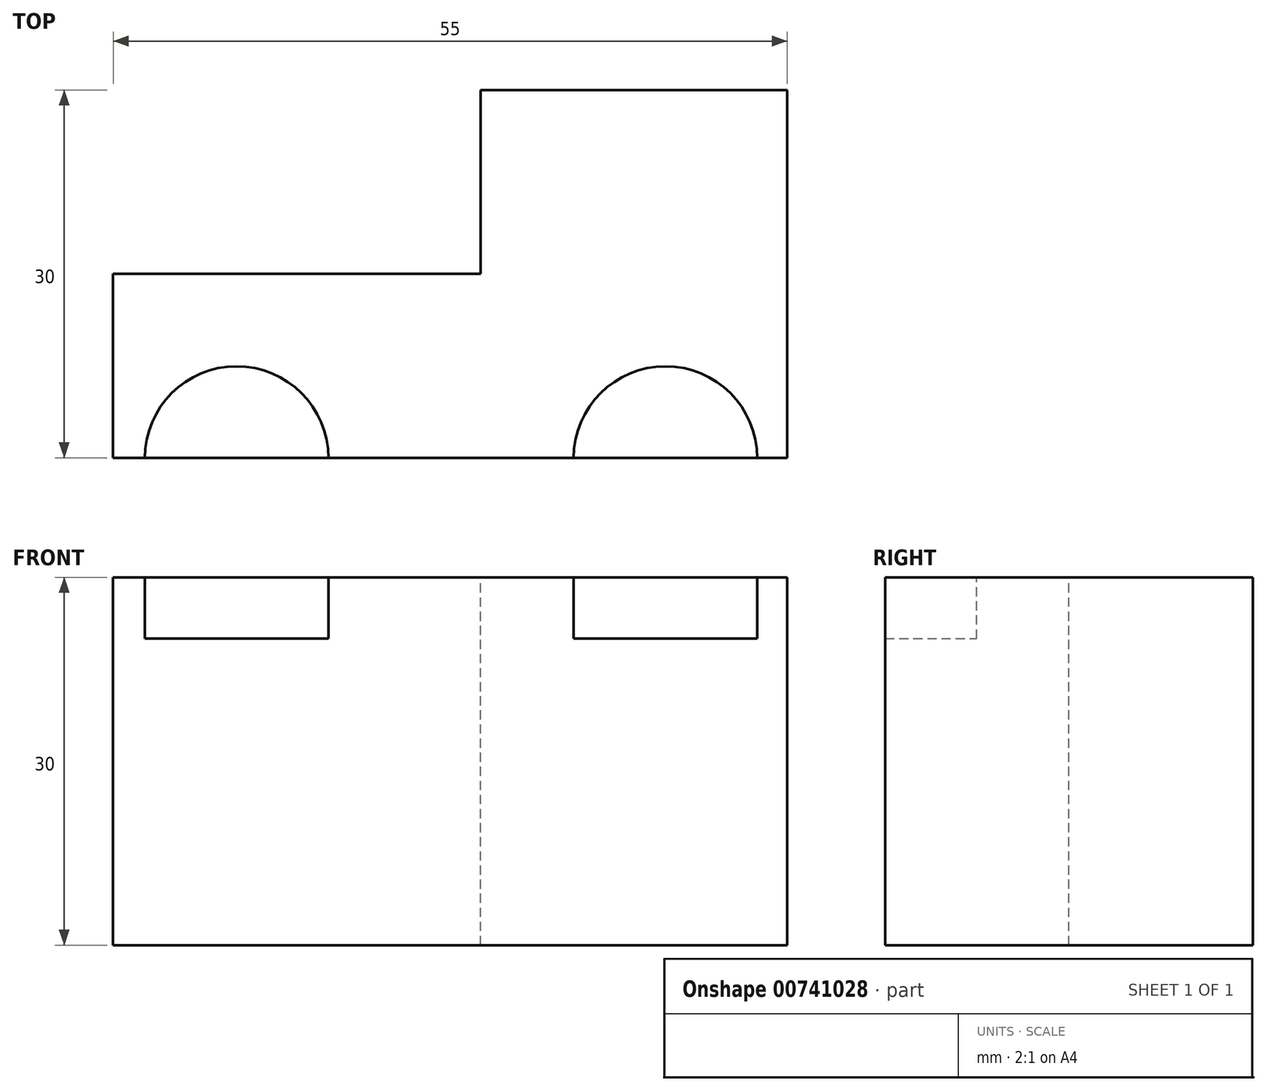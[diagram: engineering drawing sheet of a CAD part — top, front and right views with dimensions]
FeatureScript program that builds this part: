
annotation { "Feature Type Name" : "Feature", "Feature Type Description" : "" }
export const myFeature = defineFeature(function(context is Context, id is Id, definition is map)
    precondition{}
    {
        {
            var Q0;
            Q0=qCreatedBy(makeId("Top.planeOp"),FACE);
            var sketch = newSketch(context, id + "F0", { "sketchPlane" : qUnion([Q0])});
            skLineSegment(sketch, "E0.bottom", {"start": v(29.37, -15) * mm, "end": v(-25.63, -15) * mm});
            skLineSegment(sketch, "E0.top", {"start": v(29.37, 15) * mm, "end": v(-25.63, 15) * mm});
            skLineSegment(sketch, "E0.left", {"start": v(29.37, -15) * mm, "end": v(29.37, 15) * mm});
            skLineSegment(sketch, "E0.right", {"start": v(-25.63, -15) * mm, "end": v(-25.63, 15) * mm});
            skPoint(sketch, "E0.middle", {"position": v(1.87, 0) * mm});
            skLineSegment(sketch, "E1", {"start": v(-25.63, 0) * mm, "end": v(4.37, 0) * mm});
            skLineSegment(sketch, "E2", {"start": v(4.37, 0) * mm, "end": v(4.37, 15) * mm});
            skSolve(sketch);
        }
        {
            var Q0;
            {var subQ1=sQuery(id+"F0.wireOp",EDGE,"E0.bottom");Q0=makeQuery(id+"F0.imprint","IMPRINT",FACE,{"disambiguationData":[TD([[makeQuery(id+"F0.imprint","IMPRINT",EDGE,{"derivedFrom":subQ1}),-1.0]])]});}
            extrude(context, id + "F1", {"entities" : qUnion([Q0]), "endBound" : BoundingType.SYMMETRIC, "oppositeDirection" : true, "depth" : 30 * mm, "offsetDistance" : 25 * mm});
        }
        {
            var Q0;
            Q0=makeQuery(id+"F1.opExtrude","CAP_FACE",FACE,{"disambiguationData":[OSD([sQuery(id+"F0.wireOp",EDGE,"E0.bottom"),sQuery(id+"F0.wireOp",EDGE,"E0.top"),sQuery(id+"F0.wireOp",EDGE,"E0.left"),sQuery(id+"F0.wireOp",EDGE,"E0.right"),sQuery(id+"F0.wireOp",EDGE,"E1"),sQuery(id+"F0.wireOp",EDGE,"E2")])],"isStart":true});
            var sketch = newSketch(context, id + "F2", { "sketchPlane" : qUnion([Q0])});
            skCircle(sketch, "E3", {"center": v(-15.56, -15.04) * mm, "radius": 7.5 * mm});
            skCircle(sketch, "E4.1.0.0", {"center": v(19.44, -15.04) * mm, "radius": 7.5 * mm});
            skLineSegment(sketch, "E4.direction1", {"start": v(-15.56, -15.04) * mm, "end": v(19.44, -15.04) * mm, "construction": true});
            skSolve(sketch);
        }
        {
            var Q0;
            Q0 = qSketchRegion(id + "F2", true);
            extrude(context, id + "F3", {"entities" : qUnion([Q0]), "operationType" : NewBodyOperationType.REMOVE, "oppositeDirection" : true, "depth" : 5 * mm, "offsetDistance" : 25 * mm});
        }
    });
